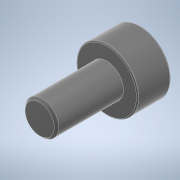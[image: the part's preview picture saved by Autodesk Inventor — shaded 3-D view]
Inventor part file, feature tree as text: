
AUTODESK INVENTOR PART (.ipt)
format: ipt  version: 2022 (Build 260153000, 153)  size: 141,312 bytes
history: native  units: in
note: dims shown in document units (in); Inventor stores cm internally (conversion verified against a paired STEP export)
features: sketch x3, extrude x2, plane x1, fillet x1, chamfer x1
ambient origin geometry x8: Origin, YZ Plane, XZ Plane, XY Plane, X Axis, Y Axis, Z Axis, Center Point
bodies: Body1 (feature_tree)
feature tree (8):
  plane  "Work Plane1"
  fillet  "Fillet1"  [1 undecoded]
  extrude  "Extrusion2"  Depth=0.0039in
  extrude  "Extrusion1"  Depth=0.2362in TaperAngle=0.0deg
  chamfer  "Chamfer1"  Distance=0.0079in
  sketch  "Sketch1"  dims[d1=0.1181in d2=0.0in d3=0.0039in]
  sketch  "Sketch2"  dims[d4=0.1181in d5=0.0in d6=0.2362in d7=0.0in d8=0.0079in d9=0.0079in d10=17.7165in]
  sketch  "Sketch3"
note: 1 required parameter value undecoded (feature->parameter linkage not recoverable at this tier; creation-order binding heuristic only, values carry confidence <= 0.55)
